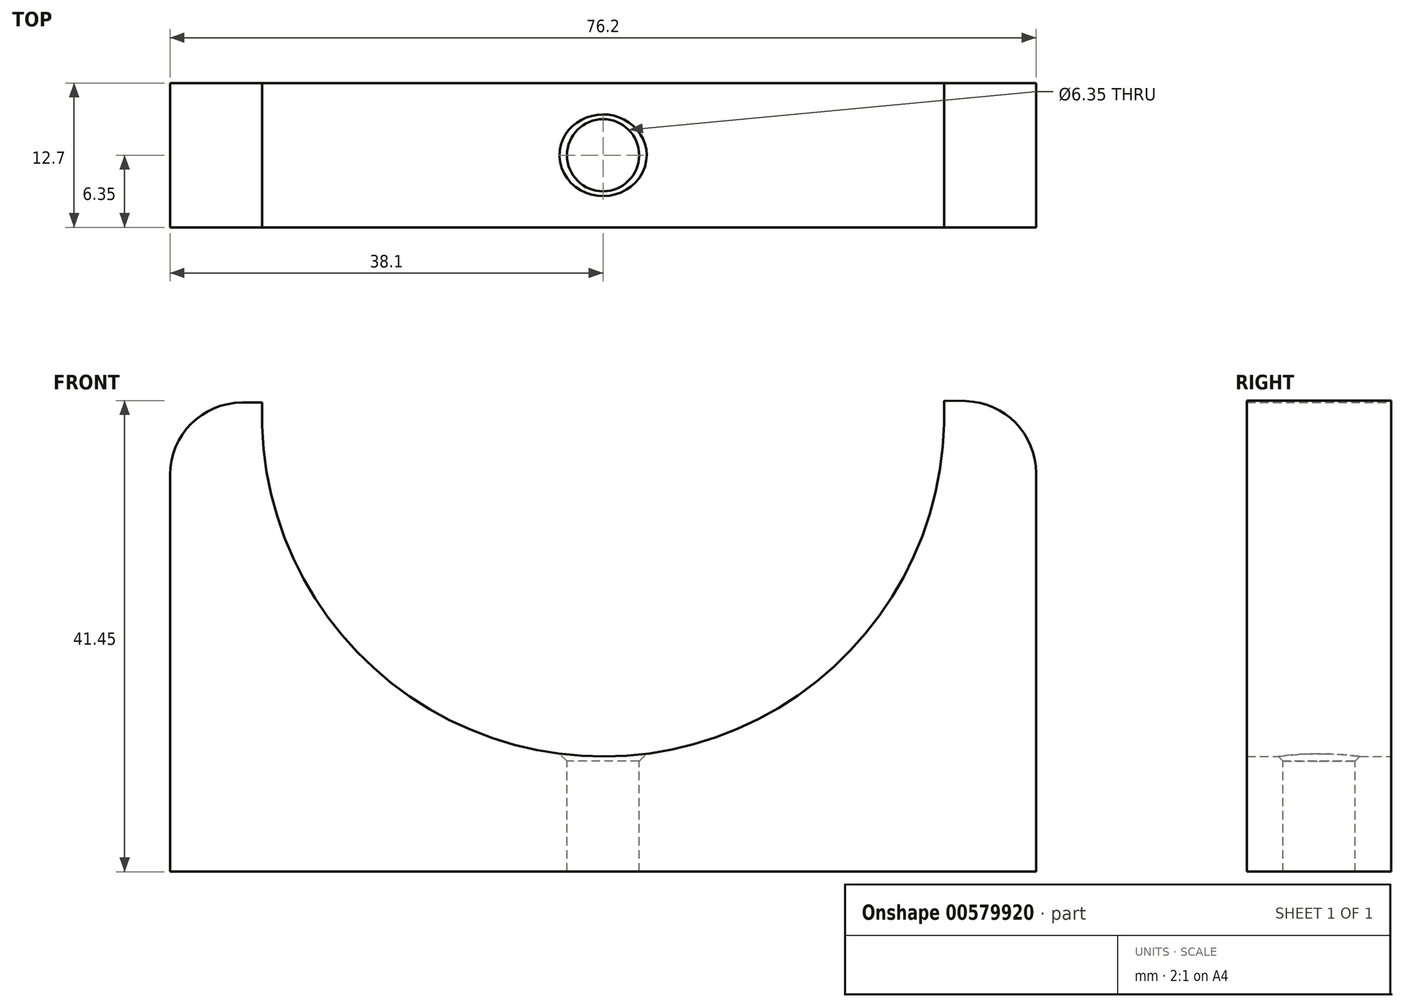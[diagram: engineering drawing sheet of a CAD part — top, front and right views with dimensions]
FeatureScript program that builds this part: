
annotation { "Feature Type Name" : "Feature", "Feature Type Description" : "" }
export const myFeature = defineFeature(function(context is Context, id is Id, definition is map)
    precondition{}
    {
        {
            var Q0;
            Q0=qCreatedBy(makeId("Front.planeOp"),FACE);
            var sketch = newSketch(context, id + "F0", { "sketchPlane" : qUnion([Q0])});
            skLineSegment(sketch, "E0.top", {"start": v(-38.1, -41.27) * mm, "end": v(38.1, -41.27) * mm});
            skLineSegment(sketch, "E0.left", {"start": v(-38.1, 0) * mm, "end": v(-38.1, -41.27) * mm});
            skLineSegment(sketch, "E0.right", {"start": v(38.1, 0) * mm, "end": v(38.1, -41.27) * mm});
            skArc(sketch, "E1", {"start": v(-30, 0) * mm, "mid": v(0.09, -31.14) * mm, "end": v(30, 0.17) * mm});
            skLineSegment(sketch, "E2", {"start": v(-38.1, 0) * mm, "end": v(-30, 0) * mm});
            skLineSegment(sketch, "E3", {"start": v(30, 0.17) * mm, "end": v(38.1, 0) * mm});
            skSolve(sketch);
        }
        {
            var Q0;
            Q0 = qSketchRegion(id + "F0", true);
            extrude(context, id + "F1", {"entities" : qUnion([Q0]), "depth" : 12.7 * mm, "offsetDistance" : 25.4 * mm});
        }
        {
            var Q0;
            Q0=qCreatedBy(makeId("Top.planeOp"),FACE);
            cPlane(context, id + "F2", {"entities" : qUnion([Q0]), "cplaneType" : CPlaneType.OFFSET, "offset" : 25.4 * mm, "oppositeDirection" : true, "width" : 152.4 * mm, "height" : 152.4 * mm});
        }
        {
            var Q0;
            Q0=qCreatedBy(id+"F2.planeOp",FACE);
            var sketch = newSketch(context, id + "F3", { "sketchPlane" : qUnion([Q0])});
            skCircle(sketch, "E4", {"center": v(0, -6.35) * mm, "radius": 4.76 * mm});
            skSolve(sketch);
        }
        {
            var Q0;
            Q0 = qSketchRegion(id + "F3", true);
            extrude(context, id + "F4", {"entities" : qUnion([Q0]), "operationType" : NewBodyOperationType.REMOVE, "oppositeDirection" : true, "depth" : 6.35 * mm, "offsetDistance" : 25.4 * mm});
        }
        {
            var Q0;
            Q0=makeQuery(id+"F4.boolean.opBoolean","COPY",FACE,{"derivedFrom":makeQuery(id+"F4.opExtrude","CAP_FACE",FACE,{"disambiguationData":[OSD([sQuery(id+"F3.wireOp",EDGE,"E4")])],"isStart":false})});
            var sketch = newSketch(context, id + "F5", { "sketchPlane" : qUnion([Q0])});
            skCircle(sketch, "E5", {"center": v(0, -6.35) * mm, "radius": 3.18 * mm});
            skSolve(sketch);
        }
        {
            var Q0;
            Q0 = qSketchRegion(id + "F5", true);
            extrude(context, id + "F6", {"entities" : qUnion([Q0]), "operationType" : NewBodyOperationType.REMOVE, "oppositeDirection" : true, "depth" : 12.7 * mm, "offsetDistance" : 25.4 * mm});
        }
        {
            var Q0;
            Q0=makeQuery(id+"F4.boolean.opBoolean","COPY",EDGE,{"derivedFrom":makeQuery(id+"F4.opExtrude","CAP_EDGE",EDGE,{"disambiguationData":[OSD([sQuery(id+"F3.wireOp",EDGE,"E4")])],"isStart":false})});
            chamfer(context, id + "F7", {"entities" : qUnion([Q0]), "width" : 1.78 * mm, "tangentPropagation" : true});
        }
        {
            var Q0;
            Q0=makeQuery(id+"F1.opExtrude","SWEPT_EDGE",EDGE,{"disambiguationData":[OSD([sQuery(id+"F0.wireOp",EDGE,"E0.left"),sQuery(id+"F0.wireOp",EDGE,"E2")])]});
            var Q1;
            Q1=makeQuery(id+"F1.opExtrude","SWEPT_EDGE",EDGE,{"disambiguationData":[OSD([sQuery(id+"F0.wireOp",EDGE,"E0.right"),sQuery(id+"F0.wireOp",EDGE,"E3")])]});
            fillet(context, id + "F8", {"entities" : qUnion([Q0, Q1]), "radius" : 6.35 * mm, "tangentPropagation" : true, "allowEdgeOverflow" : false});
        }
    });
